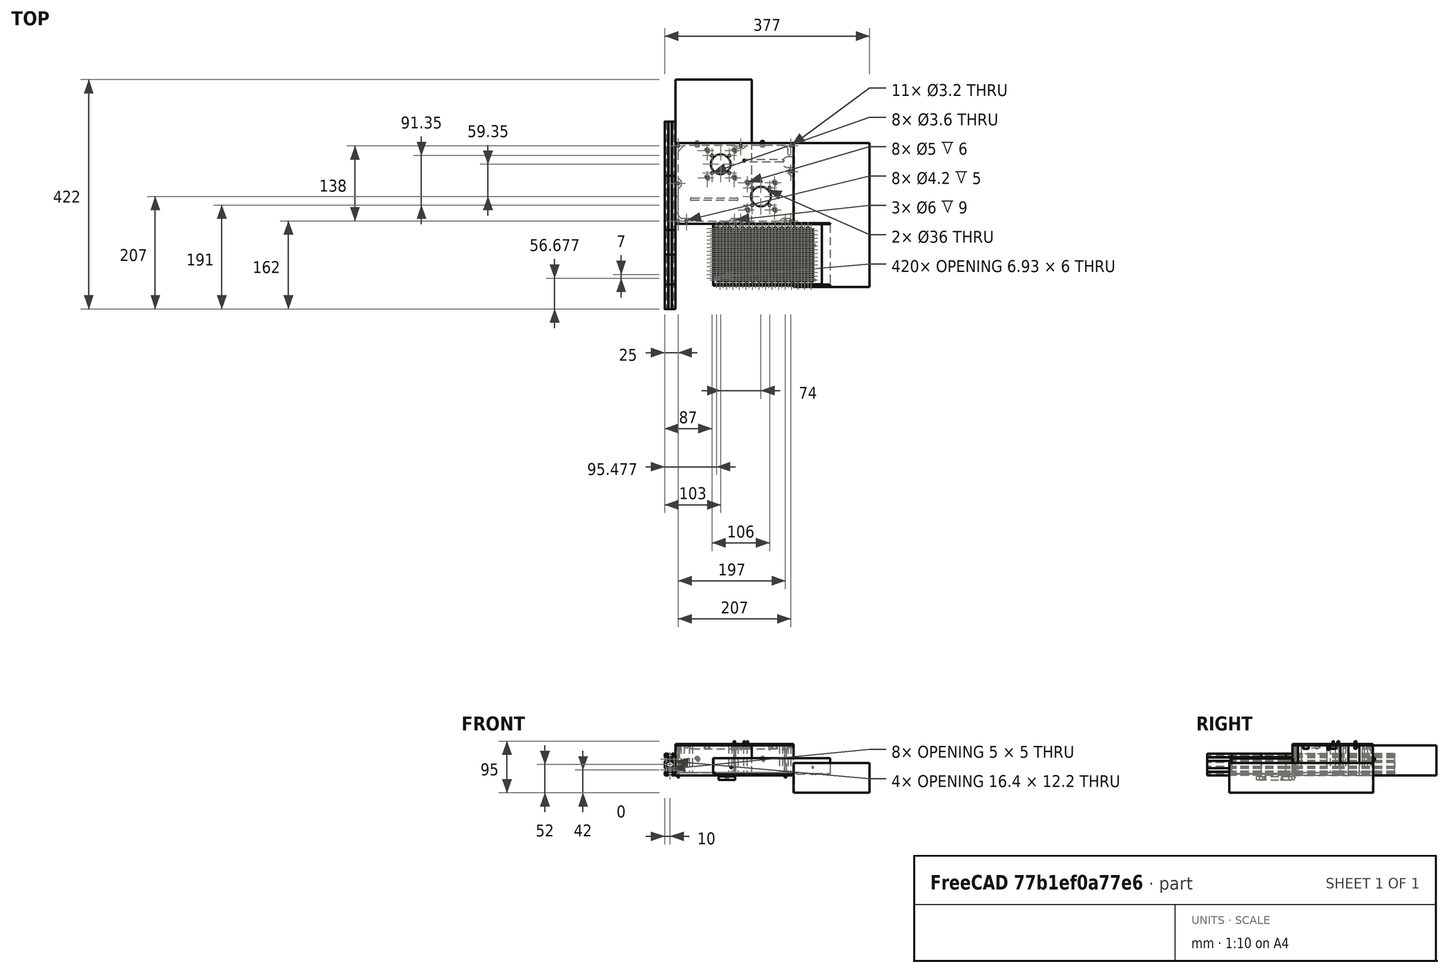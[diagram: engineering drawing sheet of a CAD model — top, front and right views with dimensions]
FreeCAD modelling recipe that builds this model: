
FCSTD DOCUMENT  (FreeCAD 0.20R29603 (Git))
Label: Electronics Enclosure
License: All rights reserved
LicenseURL: http://en.wikipedia.org/wiki/All_rights_reserved
objects: Mesh::Feature×27, Sketcher::SketchObject×12, Part::FeaturePython×10, PartDesign::Pad×6, PartDesign::Pocket×6, App::DocumentObjectGroup×6, Part::Feature×5, PartDesign::Body×4, PartDesign::ShapeBinder×1, Part::Thickness×1, PartDesign::Fillet×1, App::LinkGroup×1
note: 59 computed .brp shape members not serialized (recipe doc carries the construction recipe); baked Part::Feature solids carry a one-line shape summary decoded from their .brp

FEATURE [Sketcher::SketchObject] Sketch
  FullyConstrained = true
  MapMode = 5
  Support = -> [XY_Plane]
  sketch-geometry (8):
    g0: LineSegment StartX=0 StartY=0 StartZ=0 EndX=217 EndY=0 EndZ=0
    g1: LineSegment StartX=217 StartY=0 StartZ=0 EndX=217 EndY=103 EndZ=0
    g2: LineSegment StartX=217 StartY=148 StartZ=0 EndX=0 EndY=148 EndZ=0
    g3: LineSegment StartX=0 StartY=148 StartZ=0 EndX=0 EndY=0 EndZ=0
    g4: LineSegment StartX=217 StartY=123 StartZ=0 EndX=207 EndY=123 EndZ=0
    g5: LineSegment StartX=217 StartY=103 StartZ=0 EndX=207 EndY=103 EndZ=0
    g6: ArcOfCircle CenterX=207 CenterY=113 CenterZ=0 NormalX=0 NormalY=0 NormalZ=1 AngleXU=0 Radius=10 StartAngle=1.5708 EndAngle=4.71239
    g7: LineSegment StartX=217 StartY=123 StartZ=0 EndX=217 EndY=148 EndZ=0
  constraints (23):
    c: Coincident(g0,g1)
    c: Coincident(g7,g2)
    c: Coincident(g2,g3)
    c: Coincident(g3,g0)
    c: Horizontal(g0)
    c: Horizontal(g2)
    c: Vertical(g1)
    c: Vertical(g3)
    c: Coincident(g0,g-1)
    c: DistanceX(g0,g0) = 217
    c: DistanceY(g3,g3) = 148
    c: Horizontal(g4)
    c: Horizontal(g5)
    c: Coincident(g6,g4)
    c: Coincident(g6,g5)
    c: DistanceY(g5,g4) = 20
    c: Vertical(g4,g6)
    c: Vertical(g6,g5)
    c: DistanceY(g4,g7) = 25
    c: DistanceX(g5,g5) = 10
    c: Coincident(g1,g5)
    c: Coincident(g7,g4)
    c: Tangent(g1,g7)
FEATURE [PartDesign::Pad] Pad  label="Base"
  Direction = (1,1,1)
  Length = 5
  Length2 = 100
  Profile = -> Sketch
  Type = 0
FEATURE [Sketcher::SketchObject] Sketch001
  ExternalGeometry = -> [Pad]
  FullyConstrained = true
  MapMode = 5
  Placement = pos=(0,0,5) rot=(0,0,1;0rad)
  Support = -> [Pad]
  sketch-geometry (14):
    g0: LineSegment StartX=217 StartY=10 StartZ=0 EndX=217 EndY=0 EndZ=0
    g1: LineSegment StartX=217 StartY=0 StartZ=0 EndX=0 EndY=0 EndZ=0
    g2: LineSegment StartX=0 StartY=0 StartZ=0 EndX=0 EndY=148 EndZ=0
    g3: LineSegment StartX=0 StartY=148 StartZ=0 EndX=217 EndY=148 EndZ=0
    g4: LineSegment StartX=217 StartY=148 StartZ=0 EndX=217 EndY=123 EndZ=0
    g5: LineSegment StartX=217 StartY=123 StartZ=0 EndX=207 EndY=123 EndZ=0
    g6: LineSegment StartX=207 StartY=123 StartZ=0 EndX=207 EndY=138 EndZ=0
    g7: LineSegment StartX=207 StartY=138 StartZ=0 EndX=10 EndY=138 EndZ=0
    g8: LineSegment StartX=10 StartY=138 StartZ=0 EndX=10 EndY=10 EndZ=0
    g9: LineSegment StartX=10 StartY=10 StartZ=0 EndX=217 EndY=10 EndZ=0
    g10: LineSegment StartX=217 StartY=103 StartZ=0 EndX=207 EndY=103 EndZ=0
    g11: LineSegment StartX=207 StartY=103 StartZ=0 EndX=207 EndY=88 EndZ=0
    g12: LineSegment StartX=207 StartY=88 StartZ=0 EndX=217 EndY=88 EndZ=0
    g13: LineSegment StartX=217 StartY=88 StartZ=0 EndX=217 EndY=103 EndZ=0
  constraints (35):
    c: PointOnObject(g0,g-6)
    c: Coincident(g0,g-6)
    c: Coincident(g0,g1)
    c: Coincident(g1,g-1)
    c: Coincident(g1,g2)
    c: Coincident(g2,g-4)
    c: Coincident(g2,g3)
    c: Coincident(g3,g-4)
    c: Coincident(g3,g4)
    c: Coincident(g4,g-3)
    c: Coincident(g4,g5)
    c: Coincident(g5,g-3)
    c: Coincident(g5,g6)
    c: Vertical(g6)
    c: Coincident(g6,g7)
    c: Horizontal(g7)
    c: Coincident(g7,g8)
    c: Vertical(g8)
    c: Coincident(g8,g9)
    c: Coincident(g9,g0)
    c: Horizontal(g9)
    c: DistanceY(g0,g0) = 10
    c: DistanceY(g6,g3) = 10
    c: DistanceX(g2,g7) = 10
    c: Coincident(g10,g11)
    c: Coincident(g11,g12)
    c: Coincident(g12,g13)
    c: Coincident(g13,g10)
    c: Horizontal(g10)
    c: Horizontal(g12)
    c: Vertical(g11)
    c: Vertical(g13)
    c: Coincident(g10,g-6)
    c: Vertical(g10,g5)
    c: DistanceY(g13,g13) = 15
FEATURE [PartDesign::Pad] Pad001  label="Walls"
  BaseFeature = -> Pad
  Direction = (1,1,1)
  Length = 50
  Length2 = 100
  Profile = -> Sketch001
  Type = 0
FEATURE [Sketcher::SketchObject] Sketch002
  ExternalGeometry = -> [Pad001]
  FullyConstrained = true
  MapMode = 5
  Placement = pos=(0,0,55) rot=(0,0,1;0rad)
  Support = -> [Pad001]
  sketch-geometry (3):
    g0: Circle CenterX=5 CenterY=5 CenterZ=0 NormalX=0 NormalY=0 NormalZ=1 AngleXU=0 Radius=1.6
    g1: Circle CenterX=108.5 CenterY=5 CenterZ=0 NormalX=0 NormalY=0 NormalZ=1 AngleXU=0 Radius=1.6
    g2: Circle CenterX=202 CenterY=5 CenterZ=0 NormalX=0 NormalY=0 NormalZ=1 AngleXU=0 Radius=1.6
  constraints (10):
    c: Horizontal(g0,g1)
    c: Horizontal(g1,g2)
    c: Radius(g0) = 1.6
    c: Equal(g0,g1)
    c: Equal(g1,g2)
    c: DistanceY(g-1,g0) = 5
    c: DistanceX(g-1,g0) = 5
    c: DistanceX(g2,g-3) = 5
    c: DistanceX(g-1,g1) = 108.5
    c: DistanceX(g1,g-3) = 98.5
FEATURE [PartDesign::Pocket] Pocket  label="Center mounting holes"
  BaseFeature = -> Pad001
  Direction = (1,1,1)
  Length = 55
  Length2 = 100
  Profile = -> Sketch002
  Type = 0
FEATURE [Sketcher::SketchObject] Sketch003
  ExternalGeometry = -> [Pocket]
  FullyConstrained = true
  MapMode = 5
  Placement = pos=(0,0,55) rot=(0,0,1;0rad)
  Support = -> [Pocket]
  sketch-geometry (3):
    g0: Circle CenterX=5 CenterY=5 CenterZ=0 NormalX=0 NormalY=0 NormalZ=1 AngleXU=0 Radius=3
    g1: Circle CenterX=108.5 CenterY=5 CenterZ=0 NormalX=0 NormalY=0 NormalZ=1 AngleXU=0 Radius=3
    g2: Circle CenterX=202 CenterY=5 CenterZ=0 NormalX=0 NormalY=0 NormalZ=1 AngleXU=0 Radius=3
  constraints (6):
    c: Coincident(g0,g-3)
    c: Coincident(g1,g-4)
    c: Coincident(g2,g-5)
    c: Radius(g0) = 3
    c: Equal(g0,g1)
    c: Equal(g1,g2)
FEATURE [PartDesign::Pocket] Pocket001  label="Center Recess"
  BaseFeature = -> Pocket
  Direction = (1,1,1)
  Length = 9
  Length2 = 100
  Profile = -> Sketch003
  Type = 0
FEATURE [Mesh::Feature] _040_Profile___200mm  label="4040_Profile_-_200mm"
  Placement = pos=(8.9e-15,148,40) rot=(0,1,0;1.5708rad)
FEATURE [Sketcher::SketchObject] Sketch004
  FullyConstrained = true
  MapMode = 5
  Placement = pos=(0,138,0) rot=(1,0,0;1.5708rad)
  Support = -> [Pocket001]
  sketch-geometry (2):
    g0: Circle CenterX=40 CenterY=30 CenterZ=0 NormalX=0 NormalY=0 NormalZ=1 AngleXU=0 Radius=2.6
    g1: Circle CenterX=160 CenterY=30 CenterZ=0 NormalX=0 NormalY=0 NormalZ=1 AngleXU=0 Radius=2.6
  constraints (6):
    c: Radius(g0) = 2.6
    c: Equal(g0,g1)
    c: Horizontal(g1,g0)
    c: DistanceY(g-1,g0) = 30
    c: DistanceX(g-1,g0) = 40
    c: DistanceX(g0,g1) = 120
FEATURE [PartDesign::Pocket] Pocket002  label="Mounting Holes Outside"
  BaseFeature = -> Pocket001
  Direction = (1,1,1)
  Length = 10
  Length2 = 100
  Profile = -> Sketch004
  Type = 0
FEATURE [Mesh::Feature] _040_Profile___200mm001  label="4040_Profile_-_200mm001"
  Placement = pos=(-43,-5,9e-16) rot=(0,1,0;1.5708rad)
FEATURE [Mesh::Feature] _040_Profile___200mm002  label="4040_Profile_-_200mm002"
  Placement = pos=(157,-157,40) rot=(0,1,0;1.5708rad)
FEATURE [Mesh::Feature] _040_Profile___200mm003  label="4040_Profile_-_200mm003"
  Placement = pos=(157,-5,9e-16) rot=(0,1,0;1.5708rad)
FEATURE [Part::Feature] Part__Feature  label="2040 Extrusion"
  Placement = pos=(-10,88,20) rot=(0.57735,-0.57735,0.57735;2.0944rad)
  shape: bbox 20 x 100 x 40 mm, 138 faces (baked)
FEATURE [Part::Feature] Part__Feature001  label="2040 Extrusion001"
  Placement = pos=(-10,-12,20) rot=(0.57735,-0.57735,0.57735;2.0944rad)
  shape: bbox 20 x 100 x 40 mm, 138 faces (baked)
FEATURE [Sketcher::SketchObject] Sketch005
  ExternalGeometry = -> [Pocket002]
  FullyConstrained = true
  MapMode = 5
  Placement = pos=(0,0,55) rot=(0,0,1;0rad)
  Support = -> [Pocket002]
  sketch-geometry (12):
    g0: LineSegment StartX=0 StartY=20 StartZ=0 EndX=10 EndY=20 EndZ=0
    g1: LineSegment StartX=10 StartY=20 StartZ=0 EndX=10 EndY=50 EndZ=0
    g2: LineSegment StartX=10 StartY=50 StartZ=0 EndX=0 EndY=50 EndZ=0
    g3: LineSegment StartX=0 StartY=50 StartZ=0 EndX=0 EndY=20 EndZ=0
    g4: Circle CenterX=5 CenterY=74 CenterZ=0 NormalX=0 NormalY=0 NormalZ=1 AngleXU=0 Radius=2.1
    g5: Circle CenterX=5 CenterY=143 CenterZ=0 NormalX=0 NormalY=0 NormalZ=1 AngleXU=0 Radius=2.1
    g6: Circle CenterX=20 CenterY=5 CenterZ=0 NormalX=0 NormalY=0 NormalZ=1 AngleXU=0 Radius=2.1
    g7: Circle CenterX=212 CenterY=5 CenterZ=0 NormalX=0 NormalY=0 NormalZ=1 AngleXU=0 Radius=2.1
    g8: Circle CenterX=120 CenterY=5 CenterZ=0 NormalX=0 NormalY=0 NormalZ=1 AngleXU=0 Radius=2.1
    g9: Circle CenterX=212 CenterY=95.5 CenterZ=0 NormalX=0 NormalY=0 NormalZ=1 AngleXU=0 Radius=2.1
    g10: Circle CenterX=212 CenterY=143 CenterZ=0 NormalX=0 NormalY=0 NormalZ=1 AngleXU=0 Radius=2.1
    g11: Circle CenterX=120 CenterY=143 CenterZ=0 NormalX=0 NormalY=0 NormalZ=1 AngleXU=0 Radius=2.1
  constraints (36):
    c: Coincident(g0,g1)
    c: Coincident(g1,g2)
    c: Coincident(g2,g3)
    c: Coincident(g3,g0)
    c: Horizontal(g0)
    c: Horizontal(g2)
    c: Vertical(g1)
    c: Vertical(g3)
    c: PointOnObject(g0,g-2)
    c: PointOnObject(g1,g-3)
    c: DistanceY(g-1,g0) = 20
    c: DistanceY(g3,g3) = 30
    c: Radius(g5) = 2.1
    c: Equal(g5,g4)
    c: Equal(g5,g6)
    c: Equal(g5,g8)
    c: Equal(g5,g7)
    c: Equal(g5,g9)
    c: Equal(g5,g10)
    c: Equal(g5,g11)
    c: Vertical(g4,g5)
    c: Horizontal(g6,g8)
    c: Horizontal(g8,g7)
    c: Vertical(g7,g9)
    c: Vertical(g9,g10)
    c: Horizontal(g10,g11)
    c: Horizontal(g11,g5)
    c: DistanceX(g-1,g5) = 5
    c: DistanceY(g-3,g5) = 5
    c: DistanceY(g6,g-3) = 5
    c: DistanceX(g-1,g6) = 20
    c: DistanceX(g7,g-4) = 5
    c: DistanceX(g6,g8) = 100
    c: Vertical(g8,g11)
    c: DistanceY(g9,g-6) = 7.5
    c: DistanceY(g-1,g4) = 74
FEATURE [PartDesign::Pocket] Pocket003  label="Top Mounting and Recess"
  BaseFeature = -> Pocket002
  Direction = (1,1,1)
  Length = 5
  Length2 = 12
  Profile = -> Sketch005
  Type = 0
FEATURE [Mesh::Feature] DIN_Rail_No_Interlocks
  Placement = pos=(12,58,5) rot=(0.57735,-0.57735,0.57735;4.18879rad)
FEATURE [Mesh::Feature] DIN_Rail_No_Interlocks001
  Placement = pos=(82,58,5) rot=(0.57735,-0.57735,0.57735;4.18879rad)
FEATURE [Mesh::Feature] DIN_Rail_No_Interlocks002
  Placement = pos=(142,58,5) rot=(0.57735,-0.57735,0.57735;4.18879rad)
FEATURE [Part::FeaturePython] Screw  label="M3x50-Screw"  # Fasteners workbench fastener (typed FeaturePython)
  Placement = pos=(5,5,46) rot=(0,0,1;0rad)
  baseObject = -> Body [Edge43]
  diameter = 4
  invert = false
  leftHanded = false
  length = 10
  lengthCustom = 50
  matchOuter = false
  offset = 0
  thread = false
  type = 33
FEATURE [Part::FeaturePython] Screw001  label="M3x50-Screw063"  # Fasteners workbench fastener (typed FeaturePython)
  Placement = pos=(108.5,5,46) rot=(0,0,1;0rad)
  baseObject = -> Body [Edge41]
  diameter = 4
  invert = false
  leftHanded = false
  length = 10
  lengthCustom = 50
  matchOuter = false
  offset = 0
  thread = false
  type = 33
FEATURE [Sketcher::SketchObject] Sketch007
  ExternalGeometry = -> [Pocket003]
  FullyConstrained = true
  MapMode = 5
  Placement = pos=(0,0,55) rot=(0,0,1;0rad)
  Support = -> [Pocket003]
  sketch-geometry (33):
    g0: LineSegment StartX=10 StartY=138 StartZ=0 EndX=4 EndY=132 EndZ=0
    g1: LineSegment StartX=4 StartY=132 StartZ=0 EndX=4 EndY=85 EndZ=0
    g2: LineSegment StartX=4 StartY=85 StartZ=0 EndX=10 EndY=79 EndZ=0
    g3: LineSegment StartX=10 StartY=79 StartZ=0 EndX=10 EndY=138 EndZ=0
    g4: LineSegment StartX=25 StartY=10 StartZ=0 EndX=103.5 EndY=10 EndZ=0
    g5: LineSegment StartX=103.5 StartY=10 StartZ=0 EndX=97.5 EndY=4 EndZ=0
    g6: LineSegment StartX=97.5 StartY=4 StartZ=0 EndX=31 EndY=4 EndZ=0
    g7: LineSegment StartX=31 StartY=4 StartZ=0 EndX=25 EndY=10 EndZ=0
    g8: LineSegment StartX=125 StartY=10 StartZ=0 EndX=197 EndY=10 EndZ=0
    g9: LineSegment StartX=197 StartY=10 StartZ=0 EndX=191 EndY=4 EndZ=0
    g10: LineSegment StartX=191 StartY=4 StartZ=0 EndX=131 EndY=4 EndZ=0
    g11: LineSegment StartX=131 StartY=4 StartZ=0 EndX=125 EndY=10 EndZ=0
    g12: LineSegment StartX=10 StartY=138 StartZ=0 EndX=115 EndY=138 EndZ=0
    g13: LineSegment StartX=115 StartY=138 StartZ=0 EndX=109 EndY=144 EndZ=0
    g14: LineSegment StartX=109 StartY=144 StartZ=0 EndX=16 EndY=144 EndZ=0
    g15: LineSegment StartX=16 StartY=144 StartZ=0 EndX=10 EndY=138 EndZ=0
    g16: LineSegment StartX=125 StartY=138 StartZ=0 EndX=207 EndY=138 EndZ=0
    g17: LineSegment StartX=207 StartY=138 StartZ=0 EndX=201 EndY=144 EndZ=0
    g18: LineSegment StartX=201 StartY=144 StartZ=0 EndX=131 EndY=144 EndZ=0
    g19: LineSegment StartX=131 StartY=144 StartZ=0 EndX=125 EndY=138 EndZ=0
    g20: LineSegment StartX=10 StartY=69 StartZ=0 EndX=4 EndY=63 EndZ=0
    g21: LineSegment StartX=4 StartY=63 StartZ=0 EndX=4 EndY=16 EndZ=0
    g22: LineSegment StartX=4 StartY=16 StartZ=0 EndX=10 EndY=10 EndZ=0
    g23: LineSegment StartX=10 StartY=10 StartZ=0 EndX=10 EndY=69 EndZ=0
    g24: LineSegment StartX=207 StartY=128 StartZ=0 EndX=212 EndY=123 EndZ=0
    g25: LineSegment StartX=212 StartY=123 StartZ=0 EndX=207 EndY=123 EndZ=0
    g26: LineSegment StartX=207 StartY=123 StartZ=0 EndX=207 EndY=128 EndZ=0
    g27: LineSegment StartX=212 StartY=103 StartZ=0 EndX=207 EndY=98 EndZ=0
    g28: LineSegment StartX=207 StartY=98 StartZ=0 EndX=207 EndY=103 EndZ=0
    g29: LineSegment StartX=207 StartY=103 StartZ=0 EndX=212 EndY=103 EndZ=0
    g30: LineSegment StartX=212 StartY=88 StartZ=0 EndX=207 EndY=93 EndZ=0
    g31: LineSegment StartX=207 StartY=93 StartZ=0 EndX=207 EndY=88 EndZ=0
    g32: LineSegment StartX=207 StartY=88 StartZ=0 EndX=212 EndY=88 EndZ=0
  constraints (92):
    c: Coincident(g0,g1)
    c: Coincident(g1,g2)
    c: Coincident(g2,g3)
    c: Coincident(g3,g0)
    c: Vertical(g1)
    c: Vertical(g3)
    c: Coincident(g4,g5)
    c: Coincident(g5,g6)
    c: Coincident(g6,g7)
    c: Coincident(g7,g4)
    c: Horizontal(g4)
    c: Horizontal(g6)
    c: Coincident(g8,g9)
    c: Coincident(g9,g10)
    c: Coincident(g10,g11)
    c: Coincident(g11,g8)
    c: Horizontal(g8)
    c: Horizontal(g10)
    c: Coincident(g12,g13)
    c: Coincident(g13,g14)
    c: Coincident(g14,g15)
    c: Coincident(g15,g12)
    c: Horizontal(g12)
    c: Horizontal(g14)
    c: Coincident(g16,g17)
    c: Coincident(g17,g18)
    c: Coincident(g18,g19)
    c: Coincident(g19,g16)
    c: Horizontal(g16)
    c: Horizontal(g18)
    c: DistanceX(g0,g0) = 6
    c: Coincident(g20,g21)
    c: Coincident(g21,g22)
    c: Coincident(g22,g23)
    c: Coincident(g23,g20)
    c: Vertical(g21)
    c: Vertical(g23)
    c: PointOnObject(g8,g-3)
    c: DistanceX(g-7,g8) = 5
    c: Angle(g10,g11) = 2.35619
    c: Angle(g9,g10) = 2.35619
    c: DistanceY(g-1,g9) = 4
    c: DistanceX(g8,g-8) = 5
    c: PointOnObject(g4,g-3)
    c: Angle(g6,g7) = 2.35619
    c: Angle(g5,g6) = 2.35619
    c: Horizontal(g5,g10)
    c: DistanceX(g4,g-6) = 5
    c: DistanceX(g-5,g4) = 5
    c: Angle(g22,g21) = 2.35619
    c: Angle(g21,g20) = 2.35619
    c: DistanceX(g20,g20) = 6
    c: DistanceY(g20,g-10) = 5
    c: Angle(g1,g0) = 2.35619
    c: Angle(g2,g1) = 2.35619
    c: DistanceY(g-10,g2) = 5
    c: Coincident(g0,g-11)
    c: Angle(g15,g14) = 2.35619
    c: Angle(g14,g13) = 2.35619
    c: DistanceY(g12,g14) = 6
    c: Coincident(g12,g0)
    c: DistanceX(g12,g-13) = 5
    c: Angle(g19,g18) = 2.35619
    c: Angle(g18,g17) = 2.35619
    c: Horizontal(g13,g18)
    c: DistanceX(g-13,g16) = 5
    c: Coincident(g16,g-12)
    c: PointOnObject(g24,g-17)
    c: PointOnObject(g24,g-16)
    c: Coincident(g24,g25)
    c: Coincident(g25,g-17)
    c: Coincident(g25,g26)
    c: Coincident(g26,g24)
    c: DistanceX(g25,g25) = 5
    c: Equal(g25,g26)
    c: PointOnObject(g27,g-14)
    c: Coincident(g27,g28)
    c: Coincident(g28,g-14)
    c: Vertical(g28)
    c: Coincident(g28,g29)
    c: Coincident(g29,g27)
    c: PointOnObject(g30,g-15)
    c: Coincident(g30,g31)
    c: Coincident(g31,g-15)
    c: Coincident(g31,g32)
    c: Coincident(g32,g30)
    c: Vertical(g31)
    c: Equal(g25,g29)
    c: Equal(g29,g28)
    c: Equal(g28,g31)
    c: Equal(g31,g32)
    c: Coincident(g22,g-9)
FEATURE [Part::FeaturePython] Screw005  label="M5x8-Screw001"  # Fasteners workbench fastener (typed FeaturePython)
  Placement = pos=(40,144,30) rot=(1,0,0;1.5708rad)
  baseObject = -> Body [Edge93]
  diameter = 3
  invert = false
  leftHanded = false
  length = 12
  lengthCustom = 8
  matchOuter = false
  offset = 0
  thread = false
  type = 39
FEATURE [PartDesign::Pocket] Pocket004  label="Wall Cutouts"
  BaseFeature = -> Pocket003
  Direction = (1,1,1)
  Length = 50
  Length2 = 100
  Profile = -> Sketch007
  Type = 0
FEATURE [PartDesign::Body] Body  label="Main Enclosure"
  Group = -> [Sketch,Pad,Sketch001,Pad001,Sketch002,Pocket,Sketch003,Pocket001,Sketch004,Pocket002,Sketch005,Pocket003,Sketch007,Pocket004]
  Origin = -> Origin
  Tip = -> Pocket004
FEATURE [Part::Feature] Part__Feature002  label="2040 Extrusion002"
  Placement = pos=(-10,-112,20) rot=(0.57735,-0.57735,0.57735;2.0944rad)
  shape: bbox 20 x 100 x 40 mm, 138 faces (baked)
FEATURE [Part::Feature] Part__Feature003  label="2040 Extrusion003"
  Placement = pos=(-10,-157,20) rot=(0.57735,-0.57735,0.57735;2.0944rad)
  shape: bbox 20 x 100 x 40 mm, 138 faces (baked)
FEATURE [Mesh::Feature] _040_Profile___200mm004  label="4040_Profile_-_200mm004"
  Placement = pos=(8.9e-15,-157,40) rot=(0,1,0;1.5708rad)
FEATURE [Mesh::Feature] _040_Profile___200mm005  label="4040_Profile_-_200mm005"
  Placement = pos=(157,148,40) rot=(0,1,0;1.5708rad)
FEATURE [Part::Feature] Part__Feature1009  label="Meanwell"
  Placement = pos=(198.3,166.3,-8) rot=(0,0,1;3.14159rad)
  shape: bbox 215 x 115 x 30 mm, 2574 faces (baked)
FEATURE [Mesh::Feature] pcb_din_clip_x3
  Placement = pos=(168,-92,-133.5) rot=(0,-1,0;1.5708rad)
FEATURE [Mesh::Feature] Nanopi_M1_Din_Rail_Mount  label="Nanopi M1 Din Rail Mount"
  Placement = pos=(163,58,25.5) rot=(0,0,1;0rad)
FEATURE [Mesh::Feature] Grill_V2_Spacer___4mm  label="Grill V2-Spacer - 4mm"
  Placement = pos=(-23,-181,245) rot=(0,1,0;1.5708rad)
FEATURE [Mesh::Feature] Grill_V2_Spacer___4mm001  label="Grill V2-Spacer - 4mm001"
  Placement = pos=(-23,212,-205) rot=(0.707107,0,0.707107;3.14159rad)
FEATURE [Mesh::Feature] Middle_Grill_V2  label="Middle Grill V2"
  Placement = pos=(-20,-57,64) rot=(-0.57735,-0.57735,0.57735;2.0944rad)
FEATURE [Mesh::Feature] grill_front_left
  Placement = pos=(-23,-212,140) rot=(0.57735,0.57735,-0.57735;4.18879rad)
FEATURE [Mesh::Feature] grill_front_right
  Placement = pos=(-23,24,140) rot=(0.57735,0.57735,-0.57735;4.18879rad)
FEATURE [Mesh::Feature] _a__grill_endcap_x4  label="[a]_grill_endcap_x4"
  Placement = pos=(-39,58,-80) rot=(0,1,0;4.71239rad)
FEATURE [Mesh::Feature] _a__y_idler_outter  label="[a]_y_idler_outter"
  Placement = pos=(-43,-95,92) rot=(0.57735,0.57735,-0.57735;4.18879rad)
FEATURE [App::DocumentObjectGroup] Group001  label="Profiles"
  Group = -> [Part__Feature002,Part__Feature003,_040_Profile___200mm004,_040_Profile___200mm005,_040_Profile___200mm,_040_Profile___200mm001,_040_Profile___200mm002,_040_Profile___200mm003,Part__Feature,Part__Feature001,_a__y_idler_outter]
FEATURE [Mesh::Feature] _a__grill_endcap_x005  label="[a]_grill_endcap_x005"
  Placement = pos=(-39,-246,-80) rot=(0,1,0;4.71239rad)
FEATURE [Part::FeaturePython] Screw006  label="M3x50-Screw064"  # Fasteners workbench fastener (typed FeaturePython)
  Placement = pos=(202,5,46) rot=(0,0,1;0rad)
  baseObject = -> Body [Edge47]
  diameter = 4
  invert = false
  leftHanded = false
  length = 10
  lengthCustom = 50
  matchOuter = false
  offset = 0
  thread = false
  type = 33
FEATURE [Part::FeaturePython] Screw007  label="M5x8-Screw"  # Fasteners workbench fastener (typed FeaturePython)
  Placement = pos=(160,144,30) rot=(1,0,0;1.5708rad)
  baseObject = -> Body [Edge95]
  diameter = 3
  invert = false
  leftHanded = false
  length = 12
  lengthCustom = 8
  matchOuter = false
  offset = 0
  thread = false
  type = 39
FEATURE [App::DocumentObjectGroup] Group003  label="Screws"
  Group = -> [Screw,Screw001,Screw005,Screw006,Screw007]
FEATURE [PartDesign::ShapeBinder] ShapeBinder
  Support = -> [Pocket004]
  TraceSupport = false
FEATURE [Sketcher::SketchObject] Sketch008
  ExternalGeometry = -> [ShapeBinder]
  FullyConstrained = true
  MapMode = 5
  Support = -> [XY_Plane001]
  sketch-geometry (50):
    g0: LineSegment StartX=0 StartY=0 StartZ=0 EndX=217 EndY=0 EndZ=0
    g1: LineSegment StartX=217 StartY=0 StartZ=0 EndX=217 EndY=148 EndZ=0
    g2: LineSegment StartX=217 StartY=148 StartZ=0 EndX=0 EndY=148 EndZ=0
    g3: LineSegment StartX=0 StartY=148 StartZ=0 EndX=0 EndY=0 EndZ=0
    g4: Circle CenterX=5 CenterY=74 CenterZ=0 NormalX=0 NormalY=0 NormalZ=1 AngleXU=0 Radius=1.6
    g5: Circle CenterX=5 CenterY=143 CenterZ=0 NormalX=0 NormalY=0 NormalZ=1 AngleXU=0 Radius=1.6
    g6: Circle CenterX=120 CenterY=143 CenterZ=0 NormalX=0 NormalY=0 NormalZ=1 AngleXU=0 Radius=1.6
    g7: Circle CenterX=212 CenterY=143 CenterZ=0 NormalX=0 NormalY=0 NormalZ=1 AngleXU=0 Radius=1.6
    g8: Circle CenterX=212 CenterY=95.5 CenterZ=0 NormalX=0 NormalY=0 NormalZ=1 AngleXU=0 Radius=1.6
    g9: Circle CenterX=212 CenterY=5 CenterZ=0 NormalX=0 NormalY=0 NormalZ=1 AngleXU=0 Radius=1.6
    g10: Circle CenterX=120 CenterY=5 CenterZ=0 NormalX=0 NormalY=0 NormalZ=1 AngleXU=0 Radius=1.6
    g11: Circle CenterX=20 CenterY=5 CenterZ=0 NormalX=0 NormalY=0 NormalZ=1 AngleXU=0 Radius=1.6
    g12: LineSegment StartX=63 StartY=130 StartZ=0 EndX=103 EndY=130 EndZ=0
    g13: LineSegment StartX=103 StartY=130 StartZ=0 EndX=103 EndY=90 EndZ=0
    g14: LineSegment StartX=103 StartY=90 StartZ=0 EndX=63 EndY=90 EndZ=0
    g15: LineSegment StartX=63 StartY=90 StartZ=0 EndX=63 EndY=130 EndZ=0
    g16: Circle CenterX=58 CenterY=134.35 CenterZ=0 NormalX=0 NormalY=0 NormalZ=1 AngleXU=0 Radius=1.6
    g17: Circle CenterX=108 CenterY=134.35 CenterZ=0 NormalX=0 NormalY=0 NormalZ=1 AngleXU=0 Radius=1.6
    g18: LineSegment StartX=58 StartY=134.35 StartZ=0 EndX=108 EndY=134.35 EndZ=0
    g19: Circle CenterX=58 CenterY=84.35 CenterZ=0 NormalX=0 NormalY=0 NormalZ=1 AngleXU=0 Radius=1.6
    g20: LineSegment StartX=58 StartY=134.35 StartZ=0 EndX=58 EndY=84.35 EndZ=0
    g21: Circle CenterX=108 CenterY=84.35 CenterZ=0 NormalX=0 NormalY=0 NormalZ=1 AngleXU=0 Radius=1.6
    g22: LineSegment StartX=58 StartY=84.35 StartZ=0 EndX=108 EndY=84.35 EndZ=0
    g23: Circle CenterX=83 CenterY=109.35 CenterZ=0 NormalX=0 NormalY=0 NormalZ=1 AngleXU=0 Radius=18
    g24: LineSegment StartX=137 StartY=70.65 StartZ=0 EndX=177 EndY=70.65 EndZ=0
    g25: LineSegment StartX=177 StartY=70.65 StartZ=0 EndX=177 EndY=30.65 EndZ=0
    g26: LineSegment StartX=177 StartY=30.65 StartZ=0 EndX=137 EndY=30.65 EndZ=0
    g27: LineSegment StartX=137 StartY=30.65 StartZ=0 EndX=137 EndY=70.65 EndZ=0
    g28: Circle CenterX=132 CenterY=75 CenterZ=0 NormalX=0 NormalY=0 NormalZ=1 AngleXU=0 Radius=1.6
    g29: Circle CenterX=182 CenterY=75 CenterZ=0 NormalX=0 NormalY=0 NormalZ=1 AngleXU=0 Radius=1.6
    g30: LineSegment StartX=132 StartY=75 StartZ=0 EndX=182 EndY=75 EndZ=0
    g31: Circle CenterX=132 CenterY=25 CenterZ=0 NormalX=0 NormalY=0 NormalZ=1 AngleXU=0 Radius=1.6
    g32: LineSegment StartX=132 StartY=75 StartZ=0 EndX=132 EndY=25 EndZ=0
    g33: Circle CenterX=182 CenterY=25 CenterZ=0 NormalX=0 NormalY=0 NormalZ=1 AngleXU=0 Radius=1.6
    g34: LineSegment StartX=132 StartY=25 StartZ=0 EndX=182 EndY=25 EndZ=0
    g35: Circle CenterX=157 CenterY=50 CenterZ=0 NormalX=0 NormalY=0 NormalZ=1 AngleXU=0 Radius=18
    g36: Circle CenterX=67 CenterY=125.35 CenterZ=0 NormalX=0 NormalY=0 NormalZ=1 AngleXU=0 Radius=1.8
    g37: Circle CenterX=99 CenterY=125.35 CenterZ=0 NormalX=0 NormalY=0 NormalZ=1 AngleXU=0 Radius=1.8
    g38: LineSegment StartX=67 StartY=125.35 StartZ=0 EndX=99 EndY=125.35 EndZ=0
    g39: Circle CenterX=67 CenterY=93.35 CenterZ=0 NormalX=0 NormalY=0 NormalZ=1 AngleXU=0 Radius=1.8
    g40: LineSegment StartX=67 StartY=125.35 StartZ=0 EndX=67 EndY=93.35 EndZ=0
    g41: Circle CenterX=99 CenterY=93.35 CenterZ=0 NormalX=0 NormalY=0 NormalZ=1 AngleXU=0 Radius=1.8
    g42: LineSegment StartX=67 StartY=93.35 StartZ=0 EndX=99 EndY=93.35 EndZ=0
    g43: Circle CenterX=141 CenterY=66 CenterZ=0 NormalX=0 NormalY=0 NormalZ=1 AngleXU=0 Radius=1.8
    g44: Circle CenterX=173 CenterY=66 CenterZ=0 NormalX=0 NormalY=0 NormalZ=1 AngleXU=0 Radius=1.8
    g45: LineSegment StartX=141 StartY=66 StartZ=0 EndX=173 EndY=66 EndZ=0
    g46: Circle CenterX=141 CenterY=34 CenterZ=0 NormalX=0 NormalY=0 NormalZ=1 AngleXU=0 Radius=1.8
    g47: LineSegment StartX=141 StartY=66 StartZ=0 EndX=141 EndY=34 EndZ=0
    g48: Circle CenterX=173 CenterY=34 CenterZ=0 NormalX=0 NormalY=0 NormalZ=1 AngleXU=0 Radius=1.8
    g49: LineSegment StartX=141 StartY=34 StartZ=0 EndX=173 EndY=34 EndZ=0
  constraints (120):
    c: Coincident(g0,g1)
    c: Coincident(g1,g2)
    c: Coincident(g2,g3)
    c: Coincident(g3,g0)
    c: Horizontal(g0)
    c: Horizontal(g2)
    c: Vertical(g1)
    c: Vertical(g3)
    c: Coincident(g0,g-1)
    c: DistanceY(g1,g1) = 148
    c: DistanceX(g2,g2) = 217
    c: Coincident(g4,g-10)
    c: Coincident(g5,g-3)
    c: Coincident(g6,g-4)
    c: Coincident(g7,g-5)
    c: Coincident(g8,g-6)
    c: Coincident(g9,g-7)
    c: Coincident(g10,g-8)
    c: Coincident(g11,g-9)
    c: Radius(g5) = 1.6
    c: Equal(g5, g6-g11) x6
    c: Equal(g5,g4)
    c: Coincident(g12,g13)
    c: Coincident(g13,g14)
    c: Coincident(g14,g15)
    c: Coincident(g15,g12)
    c: Horizontal(g12)
    c: Horizontal(g14)
    c: Vertical(g13)
    c: Vertical(g15)
    c: DistanceX(g14,g14) = 40
    c: DistanceY(g15,g15) = 40
    c: DistanceY(g12,g2) = 18
    c: DistanceX(g2,g12) = 63
    c: Coincident(g16,g18)
    c: Coincident(g17,g18)
    c: Distance(g18) = 50
    c: Angle(g18) = 0
    c: Coincident(g16,g20)
    c: Coincident(g19,g20)
    c: Equal(g20,g18)
    c: Perpendicular(g20,g18)
    c: Coincident(g19,g22)
    c: Coincident(g21,g22)
    c: Equal(g18,g22)
    c: Parallel(g22,g18)
    c: Radius(g16) = 1.6
    c: Equal(g16,g17)
    c: Equal(g17,g21)
    c: Equal(g21,g19)
    c: Symmetric(g19,g17,g23)
    c: Radius(g23) = 18
    c: DistanceY(g12,g16) = 4.35
    c: DistanceX(g16,g12) = 5
    c: Coincident(g24,g25)
    c: Coincident(g25,g26)
    c: Coincident(g26,g27)
    c: Coincident(g27,g24)
    c: Horizontal(g24)
    c: Horizontal(g26)
    c: Vertical(g25)
    c: Vertical(g27)
    c: Equal(g14,g26) = 40
    c: Equal(g15,g27) = 40
    c: Coincident(g28,g30)
    c: Coincident(g29,g30)
    c: Equal(g18,g30) = 50
    c: Parallel(g18,g30)
    c: Coincident(g28,g32)
    c: Coincident(g31,g32)
    c: Equal(g32,g30)
    c: Perpendicular(g32,g30)
    c: Coincident(g31,g34)
    c: Coincident(g33,g34)
    c: Equal(g30,g34)
    c: Parallel(g34,g30)
    c: Equal(g16,g28) = 1.6
    c: Equal(g28,g29)
    c: Equal(g29,g33)
    c: Equal(g33,g31)
    c: Symmetric(g31,g29,g35)
    c: Equal(g23,g35) = 18
    c: DistanceY(g24,g28) = 4.35
    c: DistanceX(g28,g24) = 5
    c: DistanceX(g35,g0) = 60
    c: DistanceY(g0,g35) = 50
    c: Radius(g36) = 1.8
    c: Radius(g37) = 1.8
    c: Coincident(g36,g38)
    c: Coincident(g37,g38)
    c: Distance(g38) = 32
    c: Angle(g38) = 0
    c: Radius(g39) = 1.8
    c: Coincident(g36,g40)
    c: Coincident(g39,g40)
    c: Equal(g40,g38)
    c: Perpendicular(g40,g38)
    c: Radius(g41) = 1.8
    c: Coincident(g39,g42)
    c: Coincident(g41,g42)
    c: Equal(g38,g42)
    c: Parallel(g42,g38)
    c: Symmetric(g39,g37,g23)
    c: Equal(g36,g43)
    c: Coincident(g43,g45)
    c: Coincident(g44,g45)
    c: Distance(g45) = 32
    c: Angle(g45) = 0
    c: Coincident(g43,g47)
    c: Coincident(g46,g47)
    c: Equal(g47,g45)
    c: Perpendicular(g47,g45)
    c: Coincident(g46,g49)
    c: Coincident(g48,g49)
    c: Equal(g45,g49)
    c: Parallel(g49,g45)
    c: Symmetric(g43,g48,g35)
    c: Equal(g46,g48)
    c: Equal(g48,g44)
    c: Equal(g44,g43)
FEATURE [PartDesign::Pad] Pad002
  Direction = (1,1,1)
  Length = 3
  Length2 = 100
  Profile = -> Sketch008
  Type = 0
FEATURE [Part::FeaturePython] Screw008  label="M3x8-Screw"  # Fasteners workbench fastener (typed FeaturePython)
  Placement = pos=(173,66,55) rot=(0,0,1;0rad)
  baseObject = -> Body001 [Edge18]
  diameter = 4
  invert = false
  leftHanded = false
  length = 10
  lengthCustom = 8
  matchOuter = false
  offset = 0
  thread = false
  type = 33
FEATURE [Part::FeaturePython] Screw012  label="M3x8-Screw483"  # Fasteners workbench fastener (typed FeaturePython)
  Placement = pos=(132,75,55) rot=(1,0,0;3.14159rad)
  baseObject = -> Body001 [Edge30]
  diameter = 4
  invert = false
  leftHanded = false
  length = 10
  lengthCustom = 8
  matchOuter = false
  offset = 0
  thread = false
  type = 33
FEATURE [Part::FeaturePython] Screw013  label="M3x8-Screw484"  # Fasteners workbench fastener (typed FeaturePython)
  Placement = pos=(126.325,116.001,55) rot=(1,0,0;3.14159rad)
  baseObject = -> Body001 [Edge36]
  diameter = 4
  invert = false
  leftHanded = false
  length = 10
  lengthCustom = 8
  matchOuter = false
  offset = 0
  thread = false
  type = 33
FEATURE [Part::FeaturePython] Screw014  label="M3x8-Screw485"  # Fasteners workbench fastener (typed FeaturePython)
  Placement = pos=(120,143,55) rot=(0,0,1;0rad)
  baseObject = -> Body001 [Edge33]
  diameter = 4
  invert = false
  leftHanded = false
  length = 10
  lengthCustom = 8
  matchOuter = false
  offset = 0
  thread = false
  type = 33
FEATURE [Part::FeaturePython] Screw015  label="M3x8-Screw486"  # Fasteners workbench fastener (typed FeaturePython)
  Placement = pos=(108,84.35,55) rot=(1,0,0;3.14159rad)
  baseObject = -> Body001 [Edge21]
  diameter = 4
  invert = false
  leftHanded = false
  length = 10
  lengthCustom = 8
  matchOuter = false
  offset = 0
  thread = false
  type = 33
FEATURE [Mesh::Feature] Foot_Extension  label="Foot Extension"
  Placement = pos=(20,168,40) rot=(0,0,1;0rad)
FEATURE [App::DocumentObjectGroup] Group005  label="Case Lid Screws"
  Group = -> [Screw008,Screw012,Screw013,Screw014,Screw015]
FEATURE [Mesh::Feature] Foot_Extension001  label="Foot Extension001"
  Placement = pos=(335,168,40) rot=(0,0,1;0rad)
FEATURE [Mesh::Feature] Foot_Extension002  label="Foot Extension002"
  Placement = pos=(335,-137,40) rot=(0,0,1;0rad)
FEATURE [Mesh::Feature] Foot_Extension003  label="Foot Extension003"
  Placement = pos=(20,-137,40) rot=(0,0,1;0rad)
FEATURE [App::DocumentObjectGroup] Group002  label="Skirt"
  Group = -> [grill_front_right,grill_front_left,Middle_Grill_V2,Grill_V2_Spacer___4mm001,Grill_V2_Spacer___4mm,_a__grill_endcap_x4,_a__grill_endcap_x005,Foot_Extension,Foot_Extension001,Foot_Extension002,Foot_Extension003]
FEATURE [Mesh::Feature] Left_Front_Case_Cover___Bended  label="Left Front Case Cover - Bended"
  Placement = pos=(217,147,22) rot=(0,0,1;3.14159rad)
FEATURE [Sketcher::SketchObject] Sketch009
  FullyConstrained = true
  MapMode = 5
  Support = -> [XY_Plane002]
  sketch-geometry (4):
    g0: LineSegment StartX=0 StartY=0 StartZ=0 EndX=140 EndY=0 EndZ=0
    g1: LineSegment StartX=140 StartY=0 StartZ=0 EndX=140 EndY=265 EndZ=0
    g2: LineSegment StartX=140 StartY=265 StartZ=0 EndX=0 EndY=265 EndZ=0
    g3: LineSegment StartX=0 StartY=265 StartZ=0 EndX=0 EndY=0 EndZ=0
  constraints (11):
    c: Coincident(g0,g1)
    c: Coincident(g1,g2)
    c: Coincident(g2,g3)
    c: Coincident(g3,g0)
    c: Horizontal(g0)
    c: Horizontal(g2)
    c: Vertical(g1)
    c: Vertical(g3)
    c: Coincident(g0,g-1)
    c: DistanceX(g0,g0) = 140
    c: DistanceY(g3,g3) = 265
FEATURE [PartDesign::Pad] Pad003
  Direction = (1,1,1)
  Length = 55
  Length2 = 100
  Profile = -> Sketch009
  Type = 0
FEATURE [Part::Thickness] Thickness
  Faces = -> Pad003 [Face5]
  Intersection = false
  Join = 0
  Mode = 0
  Placement = pos=(217,-116.5,-32) rot=(0,0,1;0rad)
  SelfIntersection = false
  Value = -1
FEATURE [PartDesign::Body] Body002
  Group = -> [Sketch009,Pad003]
  Origin = -> Origin002
  Tip = -> Pad003
FEATURE [Mesh::Feature] Ender_3_Case_Lid_PS_Cover  label="Ender 3 Case Lid PS Cover"
  Placement = pos=(15,-16,-34) rot=(1,0,0;3.14159rad)
FEATURE [Mesh::Feature] Ender_3_Case_Lid_PS_Cover001  label="Ender 3 Case Lid PS Cover001"
  Placement = pos=(89,43,-34) rot=(1,0,0;3.14159rad)
FEATURE [Sketcher::SketchObject] Sketch010
  ExternalGeometry = -> [Pad002]
  FullyConstrained = false
  MapMode = 5
  Placement = pos=(0,0,0) rot=(1,0,0;3.14159rad)
  Support = -> [Pad002]
  sketch-geometry (27):
    g0: ArcOfCircle CenterX=29.7369 CenterY=-45.1148 CenterZ=0 NormalX=0 NormalY=0 NormalZ=1 AngleXU=0 Radius=2.5 StartAngle=1.5708 EndAngle=4.71239
    g1: ArcOfCircle CenterX=112.41 CenterY=-45.1148 CenterZ=0 NormalX=0 NormalY=0 NormalZ=1 AngleXU=0 Radius=2.5 StartAngle=4.71239 EndAngle=7.85398
    g2: LineSegment StartX=29.7369 StartY=-47.6148 StartZ=0 EndX=112.41 EndY=-47.6148 EndZ=0
    g3: LineSegment StartX=29.7369 StartY=-42.6148 StartZ=0 EndX=112.41 EndY=-42.6148 EndZ=0
    g4: ArcOfCircle CenterX=126.325 CenterY=-116.001 CenterZ=0 NormalX=0 NormalY=0 NormalZ=1 AngleXU=0 Radius=2.5 StartAngle=1.5708 EndAngle=4.71239
    g5: ArcOfCircle CenterX=197.302 CenterY=-116.001 CenterZ=0 NormalX=0 NormalY=0 NormalZ=1 AngleXU=0 Radius=2.5 StartAngle=4.71239 EndAngle=7.85398
    g6: LineSegment StartX=126.325 StartY=-118.501 StartZ=0 EndX=197.302 EndY=-118.501 EndZ=0
    g7: LineSegment StartX=126.325 StartY=-113.501 StartZ=0 EndX=197.302 EndY=-113.501 EndZ=0
    g8: Circle CenterX=58 CenterY=-84.35 CenterZ=0 NormalX=0 NormalY=0 NormalZ=1 AngleXU=0 Radius=2.5
    g9: Circle CenterX=58 CenterY=-84.35 CenterZ=0 NormalX=0 NormalY=0 NormalZ=1 AngleXU=0 Radius=5
    g10: Circle CenterX=108 CenterY=-84.35 CenterZ=0 NormalX=0 NormalY=0 NormalZ=1 AngleXU=0 Radius=2.5
    g11: Circle CenterX=108 CenterY=-84.35 CenterZ=0 NormalX=0 NormalY=0 NormalZ=1 AngleXU=0 Radius=5
    g12: LineSegment StartX=58 StartY=-84.35 StartZ=0 EndX=108 EndY=-84.35 EndZ=0
    g13: Circle CenterX=58 CenterY=-134.35 CenterZ=0 NormalX=0 NormalY=0 NormalZ=1 AngleXU=0 Radius=2.5
    g14: Circle CenterX=58 CenterY=-134.35 CenterZ=0 NormalX=0 NormalY=0 NormalZ=1 AngleXU=0 Radius=5
    g15: LineSegment StartX=58 StartY=-84.35 StartZ=0 EndX=58 EndY=-134.35 EndZ=0
    g16: Circle CenterX=108 CenterY=-134.35 CenterZ=0 NormalX=0 NormalY=0 NormalZ=1 AngleXU=0 Radius=2.5
    g17: Circle CenterX=108 CenterY=-134.35 CenterZ=0 NormalX=0 NormalY=0 NormalZ=1 AngleXU=0 Radius=5
    g18: LineSegment StartX=58 StartY=-134.35 StartZ=0 EndX=108 EndY=-134.35 EndZ=0
    g19: Circle CenterX=132 CenterY=-25 CenterZ=0 NormalX=0 NormalY=0 NormalZ=1 AngleXU=0 Radius=5
    g20: Circle CenterX=132 CenterY=-25 CenterZ=0 NormalX=0 NormalY=0 NormalZ=1 AngleXU=0 Radius=2.5
    g21: Circle CenterX=182 CenterY=-25 CenterZ=0 NormalX=0 NormalY=0 NormalZ=1 AngleXU=0 Radius=2.5
    g22: Circle CenterX=182 CenterY=-25 CenterZ=0 NormalX=0 NormalY=0 NormalZ=1 AngleXU=0 Radius=5
    g23: Circle CenterX=132 CenterY=-75 CenterZ=0 NormalX=0 NormalY=0 NormalZ=1 AngleXU=0 Radius=2.5
    g24: Circle CenterX=132 CenterY=-75 CenterZ=0 NormalX=0 NormalY=0 NormalZ=1 AngleXU=0 Radius=5
    g25: Circle CenterX=182 CenterY=-75 CenterZ=0 NormalX=0 NormalY=0 NormalZ=1 AngleXU=0 Radius=2.5
    g26: Circle CenterX=182 CenterY=-75 CenterZ=0 NormalX=0 NormalY=0 NormalZ=1 AngleXU=0 Radius=5
  constraints (49):
    c: Tangent(g0,g3) = 1.5708
    c: Tangent(g0,g2) = -1.5708
    c: Tangent(g2,g1) = -1.5708
    c: Tangent(g3,g1) = 1.5708
    c: Horizontal(g2)
    c: Equal(g0,g1)
    c: Tangent(g4,g7) = 1.5708
    c: Tangent(g4,g6) = -1.5708
    c: Tangent(g6,g5) = -1.5708
    c: Tangent(g7,g5) = 1.5708
    c: Horizontal(g6)
    c: Equal(g4,g5)
    c: DistanceY(g4,g4) = 5
    c: DistanceY(g1,g1) = 5
    c: Coincident(g8,g-5)
    c: Coincident(g9,g8)
    c: Radius(g9) = 5
    c: Radius(g8) = 2.5
    c: Coincident(g11,g10)
    c: Radius(g11) = 5
    c: Radius(g10) = 2.5
    c: Coincident(g8,g12)
    c: Coincident(g10,g12)
    c: Distance(g12) = 50
    c: Angle(g12) = 0
    c: Coincident(g14,g13)
    c: Radius(g14) = 5
    c: Radius(g13) = 2.5
    c: Coincident(g8,g15)
    c: Coincident(g13,g15)
    c: Equal(g15,g12)
    c: Perpendicular(g15,g12)
    c: Coincident(g17,g16)
    c: Radius(g17) = 5
    c: Radius(g16) = 2.5
    c: Coincident(g13,g18)
    c: Coincident(g16,g18)
    c: Equal(g12,g18)
    c: Parallel(g18,g12)
    c: Coincident(g19,g20)
    c: Equal(g9,g19) = 5
    c: Equal(g8,g20) = 2.5
    c: Coincident(g20,g-9)
    c: Coincident(g22,g21)
    c: Coincident(g22,g-10)
    c: Coincident(g24,g23)
    c: Coincident(g24,g-8)
    c: Coincident(g26,g25)
    c: Coincident(g26,g-3)
FEATURE [PartDesign::Pad] Pad004
  BaseFeature = -> Pad002
  Direction = (1,1,1)
  Length = 6
  Length2 = 100
  Profile = -> Sketch010
  Type = 0
FEATURE [PartDesign::Fillet] Fillet
  Base = -> Pad004 [Edge15,Face49,Edge43,Face58]
  BaseFeature = -> Pad004
  Radius = 2
  SupportTransform = false
  UseAllEdges = false
FEATURE [PartDesign::Body] Body001  label="Case Lid"
  Group = -> [Sketch008,ShapeBinder,Pad002,Sketch010,Pad004,Fillet]
  Origin = -> Origin001
  Placement = pos=(0,0,55) rot=(0,0,1;0rad)
  Tip = -> Fillet
FEATURE [App::DocumentObjectGroup] Group004  label="Case Lid Group"
  Group = -> [Body001,Group005]
FEATURE [Mesh::Feature] pcb_din_clip_x004
  Placement = pos=(99.5,-92,-133.5) rot=(0,-1,0;1.5708rad)
FEATURE [App::DocumentObjectGroup] Group  label="Electronics"
  Group = -> [pcb_din_clip_x3,Nanopi_M1_Din_Rail_Mount,DIN_Rail_No_Interlocks,DIN_Rail_No_Interlocks001,DIN_Rail_No_Interlocks002,pcb_din_clip_x004]
FEATURE [App::LinkGroup] LinkGroup  label="Assembly"
  ElementList = -> [Body,Part__Feature1009,Group001,Group,Group002,Group003,Group004]
  LinkMode = 0
  Placement = pos=(-1.52588e-05,31.3354,23.5) rot=(1,0,0;3.14159rad)
FEATURE [Sketcher::SketchObject] Sketch011
  FullyConstrained = false
  MapMode = 5
  Support = -> [XY_Plane003]
  sketch-geometry (12):
    g0: LineSegment StartX=82.5165 StartY=3.92999 StartZ=0 EndX=106.517 EndY=3.92999 EndZ=0
    g1: LineSegment StartX=109.517 StartY=0.929989 StartZ=0 EndX=109.517 EndY=-63.07 EndZ=0
    g2: LineSegment StartX=106.517 StartY=-66.07 StartZ=0 EndX=82.5165 EndY=-66.07 EndZ=0
    g3: LineSegment StartX=79.5165 StartY=-63.07 StartZ=0 EndX=79.5165 EndY=0.929989 EndZ=0
    g4: ArcOfCircle CenterX=82.5165 CenterY=0.929989 CenterZ=0 NormalX=0 NormalY=0 NormalZ=1 AngleXU=0 Radius=3 StartAngle=1.5708 EndAngle=3.14159
    g5: ArcOfCircle CenterX=106.517 CenterY=0.929989 CenterZ=0 NormalX=0 NormalY=0 NormalZ=1 AngleXU=0 Radius=3 StartAngle=0 EndAngle=1.5708
    g6: ArcOfCircle CenterX=106.517 CenterY=-63.07 CenterZ=0 NormalX=0 NormalY=0 NormalZ=1 AngleXU=0 Radius=3 StartAngle=4.71239 EndAngle=6.28319
    g7: ArcOfCircle CenterX=82.5165 CenterY=-63.07 CenterZ=0 NormalX=0 NormalY=0 NormalZ=1 AngleXU=0 Radius=3 StartAngle=3.14159 EndAngle=4.71239
    g8: Circle CenterX=94.5165 CenterY=-58.07 CenterZ=0 NormalX=0 NormalY=0 NormalZ=1 AngleXU=0 Radius=3
    g9: Circle CenterX=94.5165 CenterY=-4.07001 CenterZ=0 NormalX=0 NormalY=0 NormalZ=1 AngleXU=0 Radius=3
    g10: Circle CenterX=94.5165 CenterY=-19.37 CenterZ=0 NormalX=0 NormalY=0 NormalZ=1 AngleXU=0 Radius=1.2
    g11: Circle CenterX=94.5165 CenterY=-50.87 CenterZ=0 NormalX=0 NormalY=0 NormalZ=1 AngleXU=0 Radius=1.2
  constraints (30):
    c: Horizontal(g0)
    c: Horizontal(g2)
    c: Vertical(g1)
    c: Vertical(g3)
    c: Tangent(g3,g4) = 1.5708
    c: Tangent(g0,g4) = 1.5708
    c: Tangent(g0,g5) = 1.5708
    c: Tangent(g1,g5) = 1.5708
    c: Tangent(g1,g6) = 1.5708
    c: Tangent(g2,g6) = 1.5708
    c: Tangent(g3,g7) = 1.5708
    c: Tangent(g2,g7) = 1.5708
    c: Equal(g7,g6)
    c: Equal(g6,g5)
    c: Equal(g5,g4)
    c: Radius(g4) = 3
    c: DistanceX(g3,g1) = 30
    c: DistanceY(g2,g0) = 70
    c: Vertical(g9,g8)
    c: Equal(g9,g8)
    c: Radius(g9) = 3
    c: DistanceY(g8,g9) = 54
    c: DistanceY(g2,g8) = 8
    c: DistanceX(g3,g8) = 15
    c: Diameter(g10) = 2.4
    c: Vertical(g11,g10)
    c: Equal(g10,g11)
    c: Vertical(g11,g8)
    c: DistanceY(g11,g10) = 31.5
    c: DistanceY(g2,g11) = 15.2
FEATURE [PartDesign::Pad] Pad005
  Direction = (0,0,1)
  Length = 6
  Length2 = 10
  Profile = -> Sketch011
  ReferenceAxis = -> Sketch011 [N_Axis]
  Type = 0
FEATURE [Sketcher::SketchObject] Sketch012
  ExternalGeometry = -> [Pad005]
  FullyConstrained = true
  MapMode = 5
  Placement = pos=(0,0,0) rot=(1,0,0;3.14159rad)
  Support = -> [Pad005]
  sketch-geometry (2):
    g0: Circle CenterX=94.5165 CenterY=50.87 CenterZ=0 NormalX=0 NormalY=0 NormalZ=1 AngleXU=0 Radius=2
    g1: Circle CenterX=94.5165 CenterY=19.37 CenterZ=0 NormalX=0 NormalY=0 NormalZ=1 AngleXU=0 Radius=2
  constraints (4):
    c: Coincident(g0,g-3)
    c: Coincident(g1,g-4)
    c: Equal(g0,g1)
    c: Diameter(g0) = 4
FEATURE [PartDesign::Pocket] Pocket005
  BaseFeature = -> Pad005
  Direction = (0,0,1)
  Length = 1.6
  Length2 = 5
  Profile = -> Sketch012
  ReferenceAxis = -> Sketch012 [N_Axis]
  Type = 0
FEATURE [PartDesign::Body] Body003  label="PSU 5Vx24V mount "
  Group = -> [Sketch011,Pad005,Sketch012,Pocket005]
  Origin = -> Origin003
  Placement = pos=(0,0,-8) rot=(0,0,1;0rad)
  Tip = -> Pocket005
